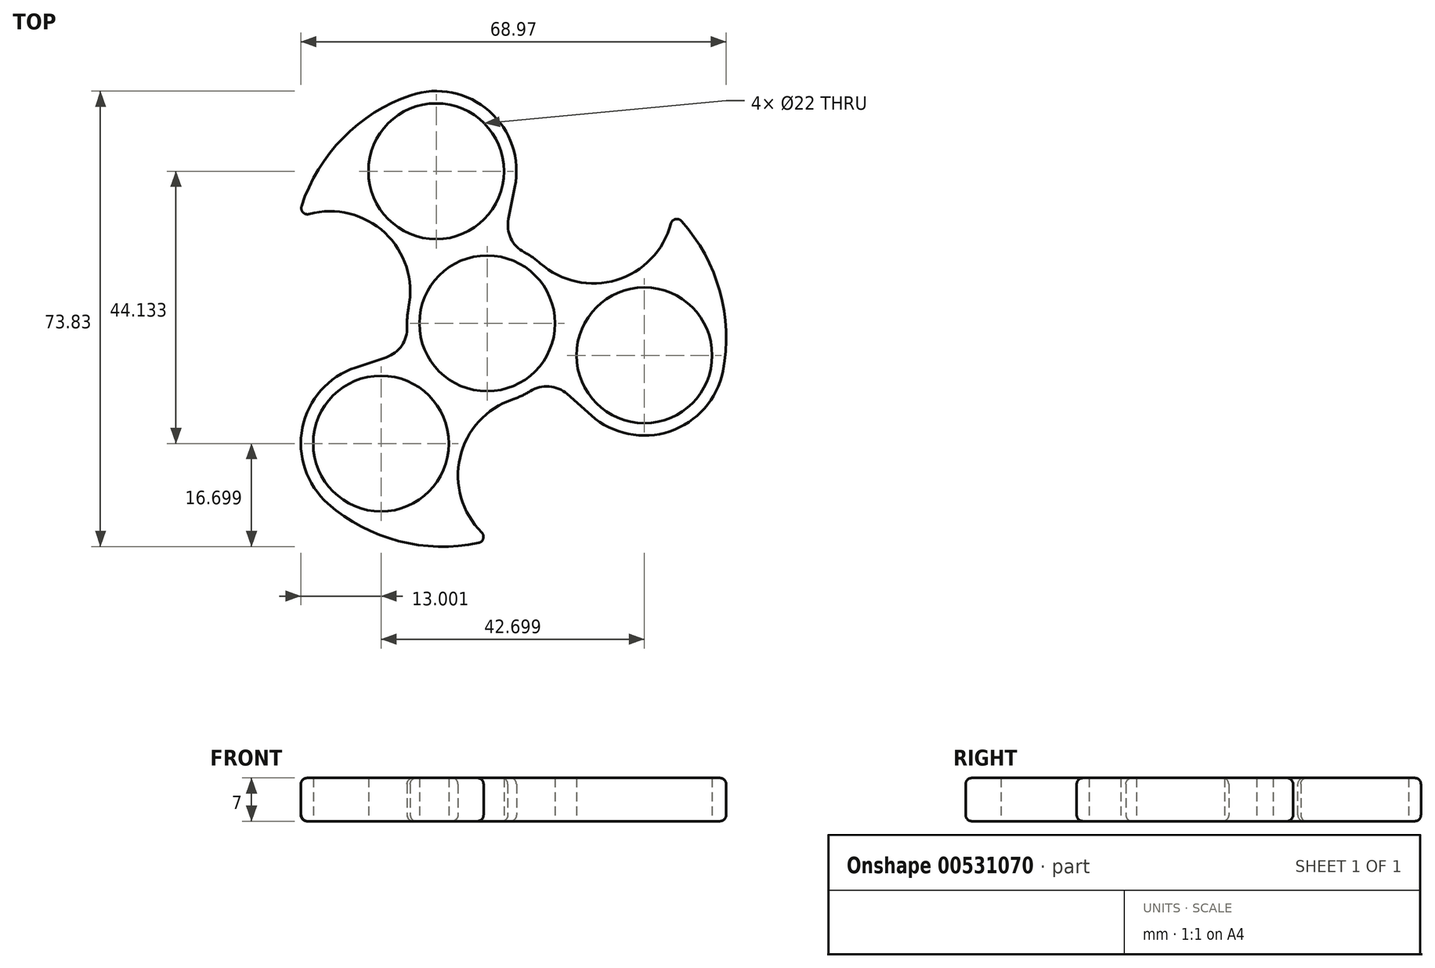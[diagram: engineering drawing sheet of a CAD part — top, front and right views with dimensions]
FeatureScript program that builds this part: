
annotation { "Feature Type Name" : "Feature", "Feature Type Description" : "" }
export const myFeature = defineFeature(function(context is Context, id is Id, definition is map)
    precondition{}
    {
        {
            var Q0;
            Q0=qCreatedBy(makeId("Top.planeOp"),FACE);
            var sketch = newSketch(context, id + "F0", { "sketchPlane" : qUnion([Q0])});
            skCircle(sketch, "E0", {"center": v(25.48, -5.17) * mm, "radius": 11 * mm});
            skCircle(sketch, "E1", {"center": v(25.48, -5.17) * mm, "radius": 13 * mm});
            skCircle(sketch, "E2", {"center": v(0, 0) * mm, "radius": 11 * mm});
            skCircle(sketch, "E3", {"center": v(0, 0) * mm, "radius": 13 * mm});
            skArc(sketch, "E4", {"start": v(38.22, -7.76) * mm, "mid": v(37.45, 6.15) * mm, "end": v(30.13, 18) * mm});
            skLineSegment(sketch, "E5", {"start": v(16.87, -14.91) * mm, "end": v(9.74, -8.6) * mm});
            skArc(sketch, "E6", {"start": v(8.6, 9.74) * mm, "mid": v(21.88, 7.34) * mm, "end": v(30.13, 18) * mm});
            skCircle(sketch, "E7.1.0", {"center": v(-8.26, 24.65) * mm, "radius": 11 * mm});
            skCircle(sketch, "E7.1.1", {"center": v(-8.26, 24.65) * mm, "radius": 13 * mm});
            skArc(sketch, "E7.1.2", {"start": v(-12.74, 2.59) * mm, "mid": v(-17.3, 15.27) * mm, "end": v(-30.66, 17.1) * mm});
            skLineSegment(sketch, "E7.1.3", {"start": v(4.48, 22.07) * mm, "end": v(2.59, 12.74) * mm});
            skArc(sketch, "E7.1.4", {"start": v(-12.4, 36.98) * mm, "mid": v(-24.05, 29.36) * mm, "end": v(-30.66, 17.1) * mm});
            skCircle(sketch, "E7.2.0", {"center": v(-17.22, -19.48) * mm, "radius": 11 * mm});
            skCircle(sketch, "E7.2.1", {"center": v(-17.22, -19.48) * mm, "radius": 13 * mm});
            skArc(sketch, "E7.2.2", {"start": v(4.13, -12.33) * mm, "mid": v(-4.58, -22.62) * mm, "end": v(0.52, -35.1) * mm});
            skLineSegment(sketch, "E7.2.3", {"start": v(-21.35, -7.15) * mm, "end": v(-12.33, -4.13) * mm});
            skArc(sketch, "E7.2.4", {"start": v(-25.83, -29.22) * mm, "mid": v(-13.4, -35.5) * mm, "end": v(0.52, -35.1) * mm});
            skSolve(sketch);
        }
        {
            var Q0;
            Q0=makeQuery(id+"F0.imprint","IMPRINT",FACE,{"disambiguationData":[TD([[makeQuery(id+"F0.imprint","IMPRINT",EDGE,{"derivedFrom":sQuery(id+"F0.wireOp",EDGE,"E0")}),-1.0]])]});
            var Q1;
            {var subQ0=sQuery(id+"F0.wireOp",EDGE,"E5");Q1=makeQuery(id+"F0.imprint","IMPRINT",FACE,{"disambiguationData":[TD([[makeQuery(id+"F0.imprint","IMPRINT",EDGE,{"derivedFrom":subQ0}),-1.0]])]});}
            var Q2;
            Q2=makeQuery(id+"F0.imprint","IMPRINT",FACE,{"disambiguationData":[TD([[makeQuery(id+"F0.imprint","IMPRINT",EDGE,{"derivedFrom":sQuery(id+"F0.wireOp",EDGE,"E2")}),-1.0]])]});
            var Q3;
            {var subQ0=sQuery(id+"F0.wireOp",EDGE,"E7.2.2");var subQ1=sQuery(id+"F0.wireOp",EDGE,"E3");var subQ2=makeQuery(id+"F0.imprint","INTERSECT",VERTEX,{"derivedFrom":[subQ1,subQ0]});Q3=makeQuery(id+"F0.imprint","IMPRINT",FACE,{"disambiguationData":[TD([[makeQuery(id+"F0.imprint","IMPRINT",EDGE,{"disambiguationData":[TD([[subQ2,1.0]])],"derivedFrom":subQ1}),-1.0]])]});}
            var Q4;
            Q4=makeQuery(id+"F0.imprint","IMPRINT",FACE,{"disambiguationData":[TD([[makeQuery(id+"F0.imprint","IMPRINT",EDGE,{"derivedFrom":sQuery(id+"F0.wireOp",EDGE,"E7.2.0")}),-1.0]])]});
            var Q5;
            {var subQ0=sQuery(id+"F0.wireOp",EDGE,"E7.2.2");var subQ1=sQuery(id+"F0.wireOp",EDGE,"E7.2.1");var subQ2=makeQuery(id+"F0.imprint","INTERSECT",VERTEX,{"derivedFrom":[subQ1,subQ0]});Q5=makeQuery(id+"F0.imprint","IMPRINT",FACE,{"disambiguationData":[TD([[makeQuery(id+"F0.imprint","IMPRINT",EDGE,{"disambiguationData":[TD([[subQ2,1.0]])],"derivedFrom":subQ1}),-1.0]])]});}
            var Q6;
            {var subQ0=sQuery(id+"F0.wireOp",EDGE,"E7.2.3");Q6=makeQuery(id+"F0.imprint","IMPRINT",FACE,{"disambiguationData":[TD([[makeQuery(id+"F0.imprint","IMPRINT",EDGE,{"derivedFrom":subQ0}),-1.0]])]});}
            var Q7;
            {var subQ0=sQuery(id+"F0.wireOp",EDGE,"E7.1.2");var subQ1=sQuery(id+"F0.wireOp",EDGE,"E3");var subQ2=makeQuery(id+"F0.imprint","INTERSECT",VERTEX,{"derivedFrom":[subQ1,subQ0]});Q7=makeQuery(id+"F0.imprint","IMPRINT",FACE,{"disambiguationData":[TD([[makeQuery(id+"F0.imprint","IMPRINT",EDGE,{"disambiguationData":[TD([[subQ2,1.0]])],"derivedFrom":subQ1}),-1.0]])]});}
            var Q8;
            Q8=makeQuery(id+"F0.imprint","IMPRINT",FACE,{"disambiguationData":[TD([[makeQuery(id+"F0.imprint","IMPRINT",EDGE,{"derivedFrom":sQuery(id+"F0.wireOp",EDGE,"E7.1.0")}),-1.0]])]});
            var Q9;
            {var subQ0=sQuery(id+"F0.wireOp",EDGE,"E7.1.2");var subQ1=sQuery(id+"F0.wireOp",EDGE,"E7.1.1");var subQ2=makeQuery(id+"F0.imprint","INTERSECT",VERTEX,{"derivedFrom":[subQ1,subQ0]});Q9=makeQuery(id+"F0.imprint","IMPRINT",FACE,{"disambiguationData":[TD([[makeQuery(id+"F0.imprint","IMPRINT",EDGE,{"disambiguationData":[TD([[subQ2,1.0]])],"derivedFrom":subQ1}),-1.0]])]});}
            var Q10;
            {var subQ0=sQuery(id+"F0.wireOp",EDGE,"E7.1.3");Q10=makeQuery(id+"F0.imprint","IMPRINT",FACE,{"disambiguationData":[TD([[makeQuery(id+"F0.imprint","IMPRINT",EDGE,{"derivedFrom":subQ0}),-1.0]])]});}
            var Q11;
            {var subQ0=sQuery(id+"F0.wireOp",EDGE,"E6");var subQ1=sQuery(id+"F0.wireOp",EDGE,"E1");var subQ2=makeQuery(id+"F0.imprint","INTERSECT",VERTEX,{"derivedFrom":[subQ1,subQ0]});Q11=makeQuery(id+"F0.imprint","IMPRINT",FACE,{"disambiguationData":[TD([[makeQuery(id+"F0.imprint","IMPRINT",EDGE,{"disambiguationData":[TD([[subQ2,1.0]])],"derivedFrom":subQ1}),-1.0]])]});}
            var Q12;
            {var subQ0=sQuery(id+"F0.wireOp",EDGE,"E6");var subQ1=sQuery(id+"F0.wireOp",EDGE,"E1");var subQ2=makeQuery(id+"F0.imprint","INTERSECT",VERTEX,{"derivedFrom":[subQ1,subQ0]});Q12=makeQuery(id+"F0.imprint","IMPRINT",FACE,{"disambiguationData":[TD([[makeQuery(id+"F0.imprint","IMPRINT",EDGE,{"disambiguationData":[TD([[subQ2,-1.0]])],"derivedFrom":subQ1}),-1.0]])]});}
            extrude(context, id + "F1", {"entities" : qUnion([Q0, Q1, Q2, Q3, Q4, Q5, Q6, Q7, Q8, Q9, Q10, Q11, Q12]), "depth" : 7 * mm, "offsetDistance" : 25 * mm});
        }
        {
            var Q0;
            Q0=makeQuery(id+"F1.opExtrude","SWEPT_EDGE",EDGE,{"disambiguationData":[OSD([sQuery(id+"F0.wireOp",EDGE,"E4"),sQuery(id+"F0.wireOp",EDGE,"E6")])]});
            var Q1;
            Q1=makeQuery(id+"F1.opExtrude","SWEPT_EDGE",EDGE,{"disambiguationData":[OSD([sQuery(id+"F0.wireOp",EDGE,"E7.2.2"),sQuery(id+"F0.wireOp",EDGE,"E7.2.4")])]});
            var Q2;
            Q2=makeQuery(id+"F1.opExtrude","SWEPT_EDGE",EDGE,{"disambiguationData":[OSD([sQuery(id+"F0.wireOp",EDGE,"E7.1.2"),sQuery(id+"F0.wireOp",EDGE,"E7.1.4")])]});
            fillet(context, id + "F2", {"entities" : qUnion([Q0, Q1, Q2]), "radius" : 1 * mm, "tangentPropagation" : true, "allowEdgeOverflow" : false});
        }
        {
            var Q0;
            Q0=makeQuery(id+"F1.opExtrude","SWEPT_EDGE",EDGE,{"disambiguationData":[OSD([sQuery(id+"F0.wireOp",EDGE,"E3"),sQuery(id+"F0.wireOp",EDGE,"E5")])]});
            var Q1;
            Q1=makeQuery(id+"F1.opExtrude","SWEPT_EDGE",EDGE,{"disambiguationData":[OSD([sQuery(id+"F0.wireOp",EDGE,"E3"),sQuery(id+"F0.wireOp",EDGE,"E7.2.3")])]});
            var Q2;
            Q2=makeQuery(id+"F1.opExtrude","SWEPT_EDGE",EDGE,{"disambiguationData":[OSD([sQuery(id+"F0.wireOp",EDGE,"E3"),sQuery(id+"F0.wireOp",EDGE,"E7.1.3")])]});
            fillet(context, id + "F3", {"entities" : qUnion([Q0, Q1, Q2]), "radius" : 5 * mm, "tangentPropagation" : true, "allowEdgeOverflow" : false});
        }
        {
            var Q0;
            Q0=makeQuery(id+"F1.opExtrude","CAP_EDGE",EDGE,{"disambiguationData":[OSD([sQuery(id+"F0.wireOp",EDGE,"E6")])],"isStart":false});
            var Q1;
            Q1=makeQuery(id+"F1.opExtrude","CAP_EDGE",EDGE,{"disambiguationData":[OSD([sQuery(id+"F0.wireOp",EDGE,"E4")])],"isStart":false});
            var Q2;
            {var subQ0=sQuery(id+"F0.wireOp",EDGE,"E6");var subQ1=sQuery(id+"F0.wireOp",EDGE,"E4");Q2=makeQuery(id+"F2.opFillet","BLEND_EDGE",EDGE,{"blendedFrom":[makeQuery(id+"F1.opExtrude","SWEPT_EDGE",EDGE,{"disambiguationData":[OSD([subQ1,subQ0])]}),makeQuery(id+"F1.opExtrude","CAP_FACE",FACE,{"disambiguationData":[OSD([sQuery(id+"F0.wireOp",EDGE,"E0"),sQuery(id+"F0.wireOp",EDGE,"E1"),sQuery(id+"F0.wireOp",EDGE,"E2"),sQuery(id+"F0.wireOp",EDGE,"E3"),subQ1,sQuery(id+"F0.wireOp",EDGE,"E5"),subQ0,sQuery(id+"F0.wireOp",EDGE,"E7.1.0"),sQuery(id+"F0.wireOp",EDGE,"E7.1.1"),sQuery(id+"F0.wireOp",EDGE,"E7.1.2"),sQuery(id+"F0.wireOp",EDGE,"E7.1.3"),sQuery(id+"F0.wireOp",EDGE,"E7.1.4"),sQuery(id+"F0.wireOp",EDGE,"E7.2.0"),sQuery(id+"F0.wireOp",EDGE,"E7.2.1"),sQuery(id+"F0.wireOp",EDGE,"E7.2.2"),sQuery(id+"F0.wireOp",EDGE,"E7.2.3"),sQuery(id+"F0.wireOp",EDGE,"E7.2.4")])],"isStart":false})],"blendedInto":[makeQuery(id+"F1.opExtrude","CAP_FACE",FACE,{"disambiguationData":[OSD([sQuery(id+"F0.wireOp",EDGE,"E0"),sQuery(id+"F0.wireOp",EDGE,"E1"),sQuery(id+"F0.wireOp",EDGE,"E2"),sQuery(id+"F0.wireOp",EDGE,"E3"),subQ1,sQuery(id+"F0.wireOp",EDGE,"E5"),subQ0,sQuery(id+"F0.wireOp",EDGE,"E7.1.0"),sQuery(id+"F0.wireOp",EDGE,"E7.1.1"),sQuery(id+"F0.wireOp",EDGE,"E7.1.2"),sQuery(id+"F0.wireOp",EDGE,"E7.1.3"),sQuery(id+"F0.wireOp",EDGE,"E7.1.4"),sQuery(id+"F0.wireOp",EDGE,"E7.2.0"),sQuery(id+"F0.wireOp",EDGE,"E7.2.1"),sQuery(id+"F0.wireOp",EDGE,"E7.2.2"),sQuery(id+"F0.wireOp",EDGE,"E7.2.3"),sQuery(id+"F0.wireOp",EDGE,"E7.2.4")])],"isStart":false})]});}
            var Q3;
            Q3=makeQuery(id+"F1.opExtrude","CAP_EDGE",EDGE,{"disambiguationData":[OSD([sQuery(id+"F0.wireOp",EDGE,"E1")])],"isStart":false});
            var Q4;
            {var subQ0=sQuery(id+"F0.wireOp",EDGE,"E5");var subQ1=sQuery(id+"F0.wireOp",EDGE,"E3");Q4=makeQuery(id+"F3.opFillet","BLEND_EDGE",EDGE,{"blendedFrom":[makeQuery(id+"F1.opExtrude","SWEPT_EDGE",EDGE,{"disambiguationData":[OSD([subQ1,subQ0])]}),makeQuery(id+"F1.opExtrude","CAP_FACE",FACE,{"disambiguationData":[OSD([sQuery(id+"F0.wireOp",EDGE,"E0"),sQuery(id+"F0.wireOp",EDGE,"E1"),sQuery(id+"F0.wireOp",EDGE,"E2"),subQ1,sQuery(id+"F0.wireOp",EDGE,"E4"),subQ0,sQuery(id+"F0.wireOp",EDGE,"E6"),sQuery(id+"F0.wireOp",EDGE,"E7.1.0"),sQuery(id+"F0.wireOp",EDGE,"E7.1.1"),sQuery(id+"F0.wireOp",EDGE,"E7.1.2"),sQuery(id+"F0.wireOp",EDGE,"E7.1.3"),sQuery(id+"F0.wireOp",EDGE,"E7.1.4"),sQuery(id+"F0.wireOp",EDGE,"E7.2.0"),sQuery(id+"F0.wireOp",EDGE,"E7.2.1"),sQuery(id+"F0.wireOp",EDGE,"E7.2.2"),sQuery(id+"F0.wireOp",EDGE,"E7.2.3"),sQuery(id+"F0.wireOp",EDGE,"E7.2.4")])],"isStart":false})],"blendedInto":[makeQuery(id+"F1.opExtrude","CAP_FACE",FACE,{"disambiguationData":[OSD([sQuery(id+"F0.wireOp",EDGE,"E0"),sQuery(id+"F0.wireOp",EDGE,"E1"),sQuery(id+"F0.wireOp",EDGE,"E2"),subQ1,sQuery(id+"F0.wireOp",EDGE,"E4"),subQ0,sQuery(id+"F0.wireOp",EDGE,"E6"),sQuery(id+"F0.wireOp",EDGE,"E7.1.0"),sQuery(id+"F0.wireOp",EDGE,"E7.1.1"),sQuery(id+"F0.wireOp",EDGE,"E7.1.2"),sQuery(id+"F0.wireOp",EDGE,"E7.1.3"),sQuery(id+"F0.wireOp",EDGE,"E7.1.4"),sQuery(id+"F0.wireOp",EDGE,"E7.2.0"),sQuery(id+"F0.wireOp",EDGE,"E7.2.1"),sQuery(id+"F0.wireOp",EDGE,"E7.2.2"),sQuery(id+"F0.wireOp",EDGE,"E7.2.3"),sQuery(id+"F0.wireOp",EDGE,"E7.2.4")])],"isStart":false})]});}
            var Q5;
            Q5=makeQuery(id+"F1.opExtrude","CAP_EDGE",EDGE,{"disambiguationData":[OSD([sQuery(id+"F0.wireOp",EDGE,"E5")])],"isStart":false});
            var Q6;
            {var subQ0=sQuery(id+"F0.wireOp",EDGE,"E7.2.4");var subQ1=sQuery(id+"F0.wireOp",EDGE,"E7.2.2");Q6=makeQuery(id+"F2.opFillet","BLEND_EDGE",EDGE,{"blendedFrom":[makeQuery(id+"F1.opExtrude","SWEPT_EDGE",EDGE,{"disambiguationData":[OSD([subQ1,subQ0])]}),makeQuery(id+"F1.opExtrude","CAP_FACE",FACE,{"disambiguationData":[OSD([sQuery(id+"F0.wireOp",EDGE,"E0"),sQuery(id+"F0.wireOp",EDGE,"E1"),sQuery(id+"F0.wireOp",EDGE,"E2"),sQuery(id+"F0.wireOp",EDGE,"E3"),sQuery(id+"F0.wireOp",EDGE,"E4"),sQuery(id+"F0.wireOp",EDGE,"E5"),sQuery(id+"F0.wireOp",EDGE,"E6"),sQuery(id+"F0.wireOp",EDGE,"E7.1.0"),sQuery(id+"F0.wireOp",EDGE,"E7.1.1"),sQuery(id+"F0.wireOp",EDGE,"E7.1.2"),sQuery(id+"F0.wireOp",EDGE,"E7.1.3"),sQuery(id+"F0.wireOp",EDGE,"E7.1.4"),sQuery(id+"F0.wireOp",EDGE,"E7.2.0"),sQuery(id+"F0.wireOp",EDGE,"E7.2.1"),subQ1,sQuery(id+"F0.wireOp",EDGE,"E7.2.3"),subQ0])],"isStart":false})],"blendedInto":[makeQuery(id+"F1.opExtrude","CAP_FACE",FACE,{"disambiguationData":[OSD([sQuery(id+"F0.wireOp",EDGE,"E0"),sQuery(id+"F0.wireOp",EDGE,"E1"),sQuery(id+"F0.wireOp",EDGE,"E2"),sQuery(id+"F0.wireOp",EDGE,"E3"),sQuery(id+"F0.wireOp",EDGE,"E4"),sQuery(id+"F0.wireOp",EDGE,"E5"),sQuery(id+"F0.wireOp",EDGE,"E6"),sQuery(id+"F0.wireOp",EDGE,"E7.1.0"),sQuery(id+"F0.wireOp",EDGE,"E7.1.1"),sQuery(id+"F0.wireOp",EDGE,"E7.1.2"),sQuery(id+"F0.wireOp",EDGE,"E7.1.3"),sQuery(id+"F0.wireOp",EDGE,"E7.1.4"),sQuery(id+"F0.wireOp",EDGE,"E7.2.0"),sQuery(id+"F0.wireOp",EDGE,"E7.2.1"),subQ1,sQuery(id+"F0.wireOp",EDGE,"E7.2.3"),subQ0])],"isStart":false})]});}
            var Q7;
            Q7=makeQuery(id+"F1.opExtrude","CAP_EDGE",EDGE,{"disambiguationData":[OSD([sQuery(id+"F0.wireOp",EDGE,"E7.2.4")])],"isStart":false});
            var Q8;
            Q8=makeQuery(id+"F1.opExtrude","CAP_EDGE",EDGE,{"disambiguationData":[OSD([sQuery(id+"F0.wireOp",EDGE,"E7.2.1")])],"isStart":false});
            var Q9;
            Q9=makeQuery(id+"F1.opExtrude","CAP_EDGE",EDGE,{"disambiguationData":[OSD([sQuery(id+"F0.wireOp",EDGE,"E7.2.3")])],"isStart":false});
            fillet(context, id + "F4", {"entities" : qUnion([Q0, Q1, Q2, Q3, Q4, Q5, Q6, Q7, Q8, Q9]), "radius" : 1 * mm, "tangentPropagation" : true, "allowEdgeOverflow" : false});
        }
        {
            var Q0;
            {var subQ0=sQuery(id+"F0.wireOp",EDGE,"E5");var subQ1=sQuery(id+"F0.wireOp",EDGE,"E3");Q0=makeQuery(id+"F3.opFillet","BLEND_EDGE",EDGE,{"blendedFrom":[makeQuery(id+"F1.opExtrude","SWEPT_EDGE",EDGE,{"disambiguationData":[OSD([subQ1,subQ0])]}),makeQuery(id+"F1.opExtrude","CAP_FACE",FACE,{"disambiguationData":[OSD([sQuery(id+"F0.wireOp",EDGE,"E0"),sQuery(id+"F0.wireOp",EDGE,"E1"),sQuery(id+"F0.wireOp",EDGE,"E2"),subQ1,sQuery(id+"F0.wireOp",EDGE,"E4"),subQ0,sQuery(id+"F0.wireOp",EDGE,"E6"),sQuery(id+"F0.wireOp",EDGE,"E7.1.0"),sQuery(id+"F0.wireOp",EDGE,"E7.1.1"),sQuery(id+"F0.wireOp",EDGE,"E7.1.2"),sQuery(id+"F0.wireOp",EDGE,"E7.1.3"),sQuery(id+"F0.wireOp",EDGE,"E7.1.4"),sQuery(id+"F0.wireOp",EDGE,"E7.2.0"),sQuery(id+"F0.wireOp",EDGE,"E7.2.1"),sQuery(id+"F0.wireOp",EDGE,"E7.2.2"),sQuery(id+"F0.wireOp",EDGE,"E7.2.3"),sQuery(id+"F0.wireOp",EDGE,"E7.2.4")])],"isStart":true})],"blendedInto":[makeQuery(id+"F1.opExtrude","CAP_FACE",FACE,{"disambiguationData":[OSD([sQuery(id+"F0.wireOp",EDGE,"E0"),sQuery(id+"F0.wireOp",EDGE,"E1"),sQuery(id+"F0.wireOp",EDGE,"E2"),subQ1,sQuery(id+"F0.wireOp",EDGE,"E4"),subQ0,sQuery(id+"F0.wireOp",EDGE,"E6"),sQuery(id+"F0.wireOp",EDGE,"E7.1.0"),sQuery(id+"F0.wireOp",EDGE,"E7.1.1"),sQuery(id+"F0.wireOp",EDGE,"E7.1.2"),sQuery(id+"F0.wireOp",EDGE,"E7.1.3"),sQuery(id+"F0.wireOp",EDGE,"E7.1.4"),sQuery(id+"F0.wireOp",EDGE,"E7.2.0"),sQuery(id+"F0.wireOp",EDGE,"E7.2.1"),sQuery(id+"F0.wireOp",EDGE,"E7.2.2"),sQuery(id+"F0.wireOp",EDGE,"E7.2.3"),sQuery(id+"F0.wireOp",EDGE,"E7.2.4")])],"isStart":true})]});}
            var Q1;
            Q1=makeQuery(id+"F1.opExtrude","CAP_EDGE",EDGE,{"disambiguationData":[OSD([sQuery(id+"F0.wireOp",EDGE,"E7.2.2")])],"isStart":true});
            var Q2;
            Q2=makeQuery(id+"F1.opExtrude","CAP_EDGE",EDGE,{"disambiguationData":[OSD([sQuery(id+"F0.wireOp",EDGE,"E7.1.2")])],"isStart":true});
            var Q3;
            Q3=makeQuery(id+"F1.opExtrude","CAP_EDGE",EDGE,{"disambiguationData":[OSD([sQuery(id+"F0.wireOp",EDGE,"E7.1.1")])],"isStart":true});
            fillet(context, id + "F5", {"entities" : qUnion([Q0, Q1, Q2, Q3]), "radius" : 1 * mm, "tangentPropagation" : true, "allowEdgeOverflow" : false});
        }
    });
